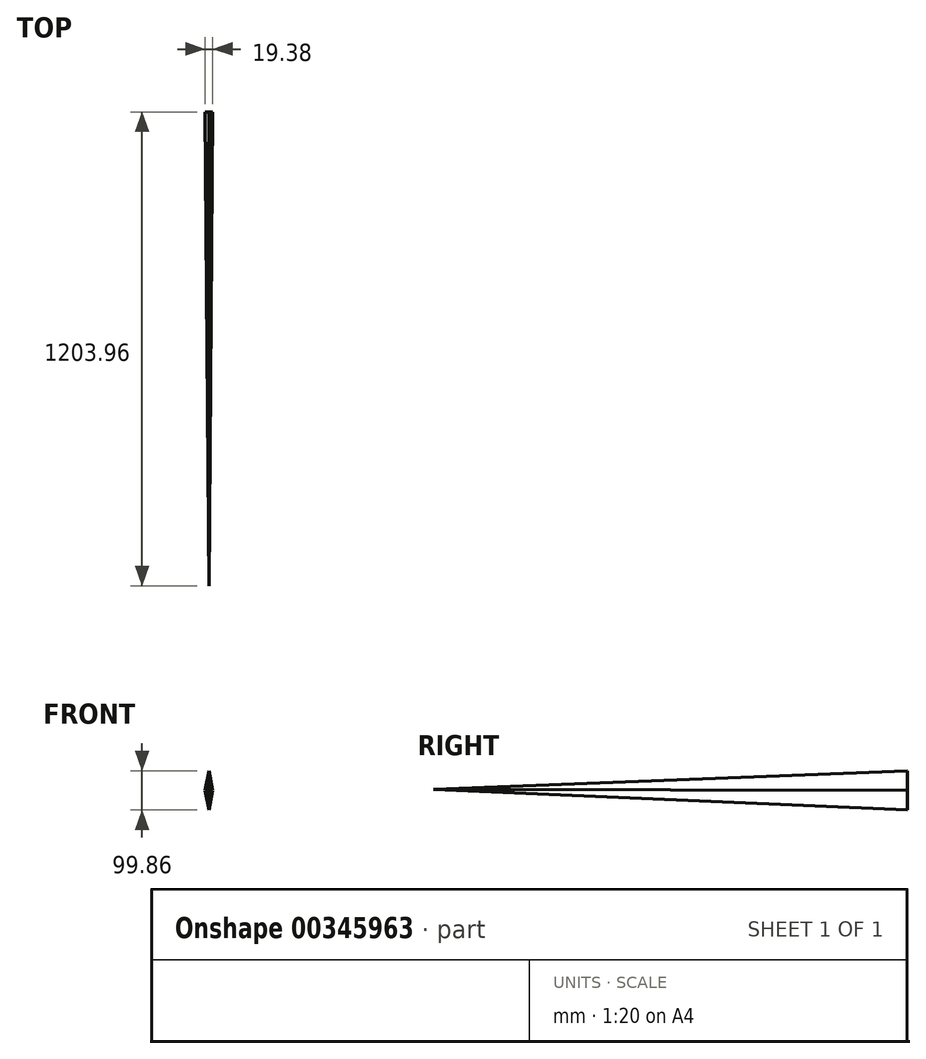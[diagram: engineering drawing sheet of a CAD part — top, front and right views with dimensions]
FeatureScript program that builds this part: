
annotation { "Feature Type Name" : "Feature", "Feature Type Description" : "" }
export const myFeature = defineFeature(function(context is Context, id is Id, definition is map)
    precondition{}
    {
        {
            var Q0;
            Q0=qCreatedBy(makeId("Front.planeOp"),FACE);
            var sketch = newSketch(context, id + "F0", { "sketchPlane" : qUnion([Q0])});
            skLineSegment(sketch, "E0", {"start": v(-9.7, 0) * mm, "end": v(0, 49.93) * mm});
            skLineSegment(sketch, "E1.MirrorCS", {"start": v(9.7, 0) * mm, "end": v(0, 49.93) * mm});
            skLineSegment(sketch, "E2.MirrorCS", {"start": v(-9.7, 0) * mm, "end": v(0, -49.93) * mm});
            skLineSegment(sketch, "E3.MirrorCS", {"start": v(9.7, 0) * mm, "end": v(0, -49.93) * mm});
            skSolve(sketch);
        }
        {
            var Q0;
            Q0=qCreatedBy(makeId("Front.planeOp"),FACE);
            cPlane(context, id + "F1", {"entities" : qUnion([Q0]), "cplaneType" : CPlaneType.OFFSET, "offset" : 1203.96 * mm, "width" : 152.4 * mm, "height" : 152.4 * mm});
        }
        {
            var Q0;
            Q0=qCreatedBy(id+"F1.planeOp",FACE);
            var sketch = newSketch(context, id + "F2", { "sketchPlane" : qUnion([Q0])});
            skLineSegment(sketch, "E4", {"start": v(-0.42, 2.26) * mm, "end": v(0, 4.53) * mm});
            skLineSegment(sketch, "E5.MirrorCS", {"start": v(0.42, 2.26) * mm, "end": v(0, 4.53) * mm});
            skLineSegment(sketch, "E6.MirrorCS", {"start": v(-0.42, 2.26) * mm, "end": v(0, 0) * mm});
            skLineSegment(sketch, "E7.MirrorCS", {"start": v(0.42, 2.26) * mm, "end": v(0, 0) * mm});
            skSolve(sketch);
        }
        {
            var Q0;
            Q0=makeQuery(id+"F0.imprint","IMPRINT",FACE,{"disambiguationData":[TD([[makeQuery(id+"F0.imprint","IMPRINT",EDGE,{"derivedFrom":sQuery(id+"F0.wireOp",EDGE,"E0")}),-1.0]])]});
            var Q1;
            Q1=sQuery(id+"F2.wireOp",VERTEX,"E5.MirrorCS.start");
            loft(context, id + "F3", {"sheetProfilesArray" : [{ "sheetProfileEntities" : qUnion([Q0]) }, { "sheetProfileEntities" : qUnion([Q1]) }]});
        }
    });
